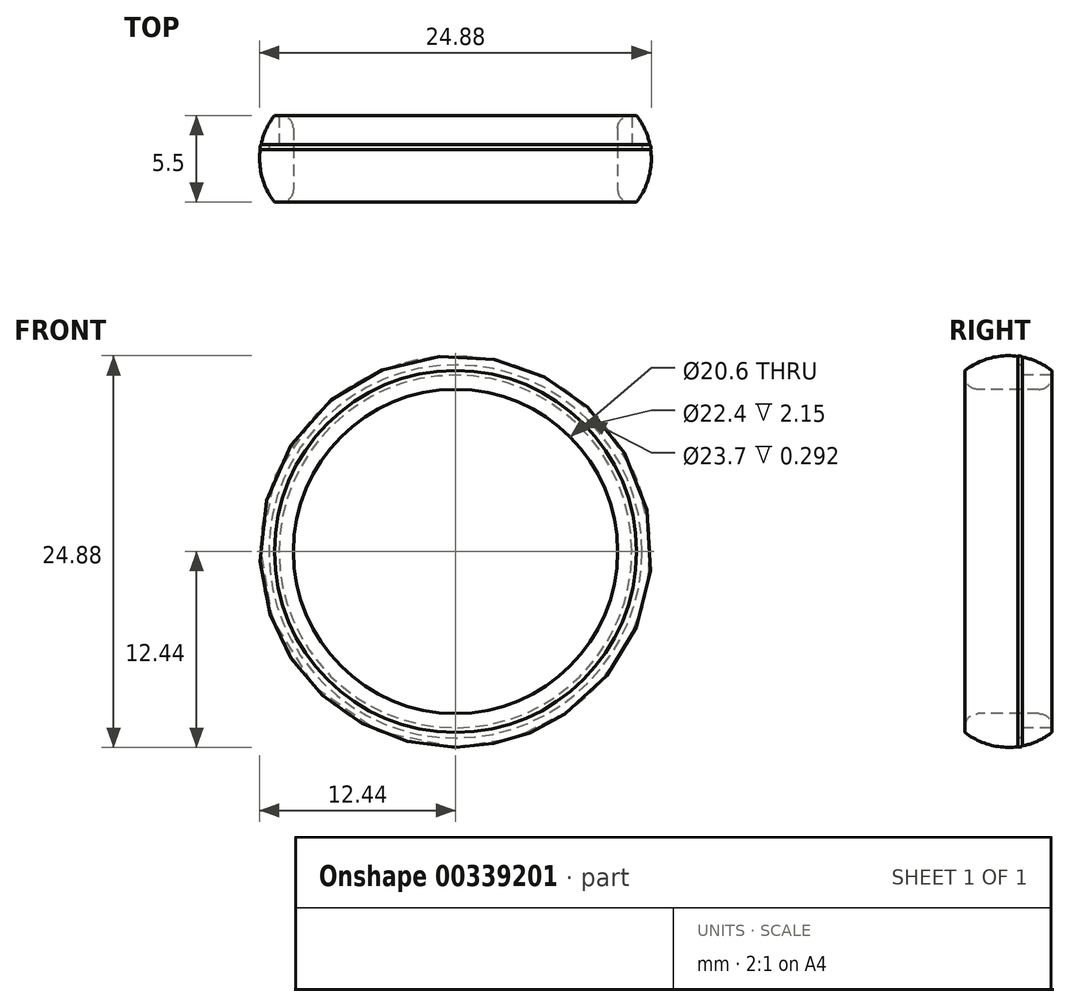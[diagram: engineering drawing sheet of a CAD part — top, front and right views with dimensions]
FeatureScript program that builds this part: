
annotation { "Feature Type Name" : "Feature", "Feature Type Description" : "" }
export const myFeature = defineFeature(function(context is Context, id is Id, definition is map)
    precondition{}
    {
        {
            var Q0;
            Q0=qCreatedBy(makeId("Front.planeOp"),FACE);
            cPlane(context, id + "F0", {"entities" : qUnion([Q0]), "cplaneType" : CPlaneType.OFFSET, "offset" : 20 * mm, "oppositeDirection" : true, "width" : 150 * mm, "height" : 150 * mm});
        }
        {
            var Q0;
            Q0=qCreatedBy(id+"F0.planeOp",FACE);
            cPlane(context, id + "F1", {"entities" : qUnion([Q0]), "cplaneType" : CPlaneType.OFFSET, "offset" : 90 * mm, "width" : 150 * mm, "height" : 150 * mm});
        }
        {
            var Q0;
            Q0=qCreatedBy(makeId("Right.planeOp"),FACE);
            var sketch = newSketch(context, id + "F2", { "sketchPlane" : qUnion([Q0])});
            skLineSegment(sketch, "E0", {"start": v(0, 0) * mm, "end": v(15.68, 0) * mm, "construction": true});
            skLineSegment(sketch, "E1", {"start": v(-2.75, 10.3) * mm, "end": v(2.75, 10.3) * mm});
            skLineSegment(sketch, "E2", {"start": v(2.75, 10.3) * mm, "end": v(2.75, 11.5) * mm});
            skLineSegment(sketch, "E3", {"start": v(-2.75, 10.3) * mm, "end": v(-2.75, 11.5) * mm});
            skLineSegment(sketch, "E4", {"start": v(-2.75, 11.5) * mm, "end": v(2.75, 11.5) * mm, "construction": true});
            skLineSegment(sketch, "E5", {"start": v(0, 10.3) * mm, "end": v(0, 0) * mm, "construction": true});
            skArc(sketch, "E6", {"start": v(2.75, 11.5) * mm, "mid": v(1.87, 12.03) * mm, "end": v(0.9, 12.35) * mm});
            skArc(sketch, "E7", {"start": v(0.6, 12.4) * mm, "mid": v(0.73, 12.25) * mm, "end": v(0.9, 12.35) * mm, "construction": true});
            skLineSegment(sketch, "E8", {"start": v(0.6, 12.4) * mm, "end": v(0.9, 12.4) * mm, "construction": true});
            skArc(sketch, "E9.trimOffspring", {"start": v(0.6, 12.4) * mm, "mid": v(-1.16, 12.28) * mm, "end": v(-2.75, 11.5) * mm});
            skArc(sketch, "E10", {"start": v(0.9, 12.35) * mm, "mid": v(0.9, 12.37) * mm, "end": v(0.9, 12.4) * mm, "construction": true});
            skLineSegment(sketch, "E11", {"start": v(0.6, 12.4) * mm, "end": v(0.6, 11.2) * mm});
            skLineSegment(sketch, "E12", {"start": v(0.9, 12.35) * mm, "end": v(0.9, 11.85) * mm});
            skLineSegment(sketch, "E13", {"start": v(0.9, 11.85) * mm, "end": v(0.6, 11.85) * mm});
            skLineSegment(sketch, "E14", {"start": v(0.6, 11.2) * mm, "end": v(2.75, 11.2) * mm});
            skArc(sketch, "E15", {"start": v(0.9, 12.35) * mm, "mid": v(0.75, 12.41) * mm, "end": v(0.6, 12.4) * mm});
            skSolve(sketch);
        }
        {
            var Q0;
            {var subQ3=sQuery(id+"F2.wireOp",EDGE,"E3");Q0=makeQuery(id+"F2.imprint","IMPRINT",FACE,{"disambiguationData":[TD([[makeQuery(id+"F2.imprint","IMPRINT",EDGE,{"derivedFrom":subQ3}),-1.0]])]});}
            var Q1;
            Q1=sQuery(id+"F2.wireOp",EDGE,"E0");
            revolve(context, id + "F3", {"entities" : qUnion([Q0]), "axis" : qUnion([Q1]), "revolveType" : RevolveType.FULL});
        }
        {
            var Q0;
            {var subQ4=sQuery(id+"F2.wireOp",EDGE,"E2");Q0=makeQuery(id+"F2.imprint","IMPRINT",FACE,{"disambiguationData":[TD([[makeQuery(id+"F2.imprint","IMPRINT",EDGE,{"derivedFrom":subQ4}),1.0]])]});}
            var Q1;
            Q1=sQuery(id+"F2.wireOp",EDGE,"E0");
            revolve(context, id + "F4", {"entities" : qUnion([Q0]), "axis" : qUnion([Q1]), "revolveType" : RevolveType.FULL});
        }
        {
            var Q0;
            Q0=makeQuery(id+"F2.imprint","IMPRINT",FACE,{"disambiguationData":[TD([[makeQuery(id+"F2.imprint","IMPRINT",EDGE,{"derivedFrom":sQuery(id+"F2.wireOp",EDGE,"E12")}),-1.0]])]});
            var Q1;
            Q1=sQuery(id+"F2.wireOp",EDGE,"E0");
            revolve(context, id + "F5", {"entities" : qUnion([Q0]), "axis" : qUnion([Q1]), "revolveType" : RevolveType.FULL});
        }
        {
            var Q0;
            Q0=makeQuery(id+"F3.opRevolve","SWEPT_EDGE",EDGE,{"disambiguationData":[OSD([sQuery(id+"F2.wireOp",EDGE,"E1"),sQuery(id+"F2.wireOp",EDGE,"E3")])]});
            var Q1;
            Q1=makeQuery(id+"F3.opRevolve","SWEPT_EDGE",EDGE,{"disambiguationData":[OSD([sQuery(id+"F2.wireOp",EDGE,"E1"),sQuery(id+"F2.wireOp",EDGE,"E2")])]});
            fillet(context, id + "F6", {"entities" : qUnion([Q0, Q1]), "radius" : .8 * mm, "tangentPropagation" : true, "allowEdgeOverflow" : false});
        }
    });
